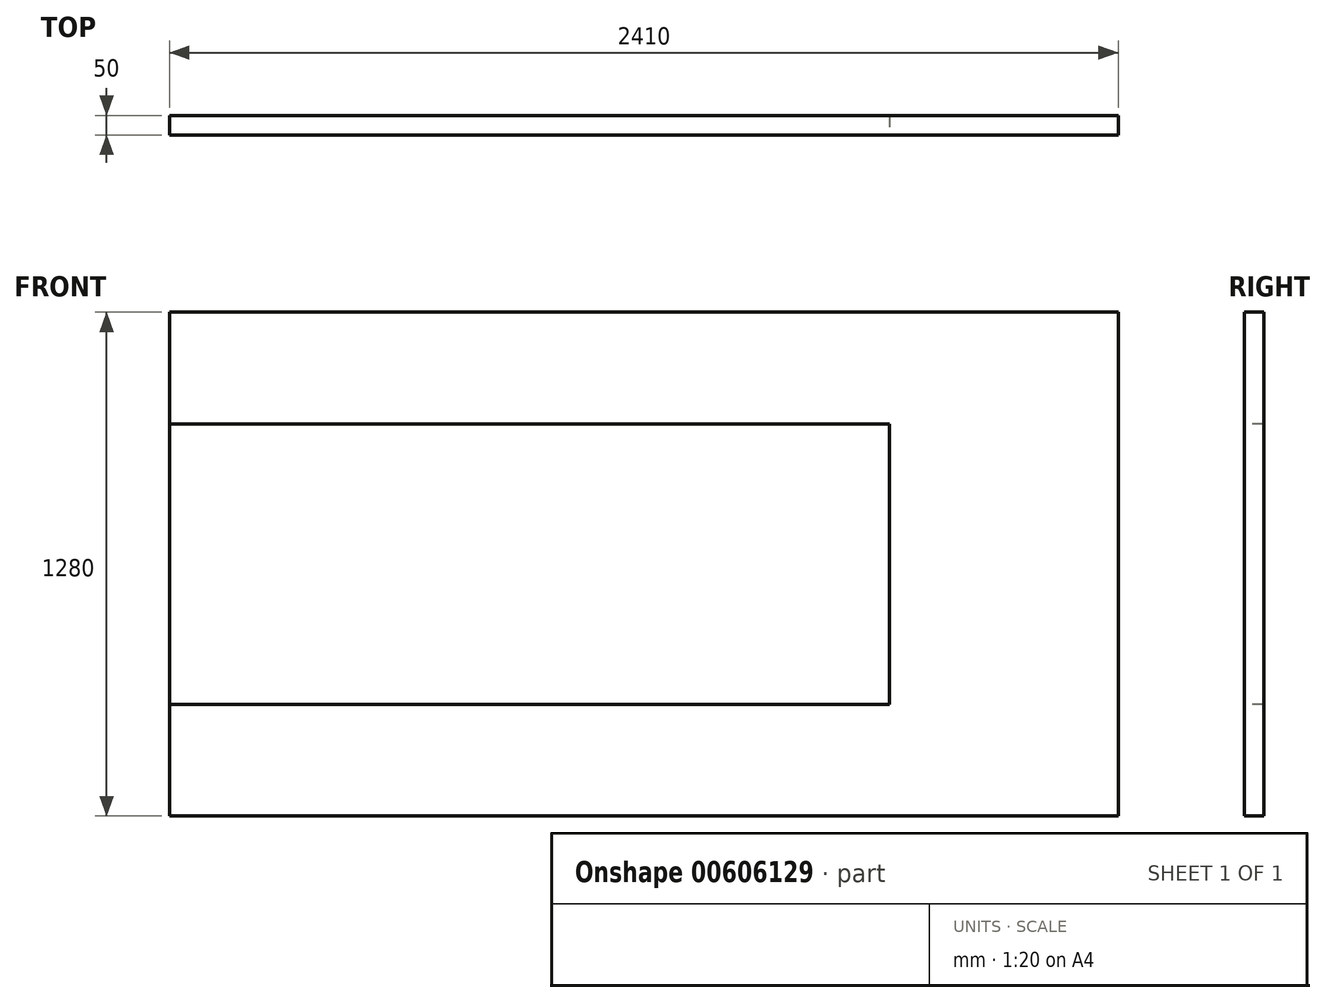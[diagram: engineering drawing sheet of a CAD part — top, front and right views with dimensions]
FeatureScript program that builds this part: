
annotation { "Feature Type Name" : "Feature", "Feature Type Description" : "" }
export const myFeature = defineFeature(function(context is Context, id is Id, definition is map)
    precondition{}
    {
        {
            var Q0;
            Q0=qCreatedBy(makeId("Front.planeOp"),FACE);
            var sketch = newSketch(context, id + "F0", { "sketchPlane" : qUnion([Q0])});
            skLineSegment(sketch, "E0.bottom", {"start": v(-1196.8, 573.64) * mm, "end": v(1213.2, 573.64) * mm});
            skLineSegment(sketch, "E0.top", {"start": v(-1196.8, -706.36) * mm, "end": v(1213.2, -706.36) * mm});
            skLineSegment(sketch, "E0.left", {"start": v(-1196.8, 573.64) * mm, "end": v(-1196.8, -706.36) * mm});
            skLineSegment(sketch, "E0.right", {"start": v(1213.2, 573.64) * mm, "end": v(1213.2, -706.36) * mm});
            skSolve(sketch);
        }
        {
            var Q0;
            Q0 = qSketchRegion(id + "F0", true);
            extrude(context, id + "F1", {"entities" : qUnion([Q0]), "depth" : 50 * mm, "offsetDistance" : 25 * mm});
        }
        {
            var Q0;
            Q0=makeQuery(id+"F1.opExtrude","CAP_FACE",FACE,{"disambiguationData":[OSD([sQuery(id+"F0.wireOp",EDGE,"E0.bottom"),sQuery(id+"F0.wireOp",EDGE,"E0.top"),sQuery(id+"F0.wireOp",EDGE,"E0.left"),sQuery(id+"F0.wireOp",EDGE,"E0.right")])],"isStart":false});
            var sketch = newSketch(context, id + "F2", { "sketchPlane" : qUnion([Q0])});
            skLineSegment(sketch, "E1.bottom", {"start": v(-1196.8, 289.64) * mm, "end": v(632.2, 289.64) * mm});
            skLineSegment(sketch, "E1.top", {"start": v(-1196.8, -422.36) * mm, "end": v(632.2, -422.36) * mm});
            skLineSegment(sketch, "E1.left", {"start": v(-1196.8, 289.64) * mm, "end": v(-1196.8, -422.36) * mm});
            skLineSegment(sketch, "E1.right", {"start": v(632.2, 289.64) * mm, "end": v(632.2, -422.36) * mm});
            skSolve(sketch);
        }
        {
            var Q0;
            Q0 = qSketchRegion(id + "F2", true);
            extrude(context, id + "F3", {"entities" : qUnion([Q0]), "oppositeDirection" : true, "depth" : 50 * mm, "offsetDistance" : 25 * mm});
        }
    });
